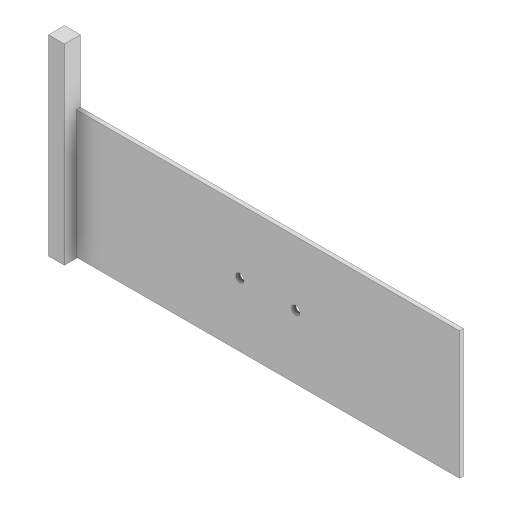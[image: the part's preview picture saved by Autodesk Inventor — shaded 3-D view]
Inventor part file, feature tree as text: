
AUTODESK INVENTOR PART (.ipt)
format: ipt  version: 2024.2 (Build 282272000, 272)  size: 103,936 bytes
history: native  units: in
note: dims shown in document units (in); Inventor stores cm internally (conversion verified against a paired STEP export)
features: extrude x2, sketch x2
ambient origin geometry x8: Origin, YZ Plane, XZ Plane, XY Plane, X Axis, Y Axis, Z Axis, Center Point
bodies: Solid1 (feature_tree)
feature tree (4):
  extrude  "Extrusion1"  Depth=4.0in
  extrude  "Extrusion2"  Depth=0.5in
  sketch  "Sketch1"  dims[d0=12.0in d1=4.0in]
  sketch  "Sketch2"  dims[d2=0.25in d3=0.25in d4=1.75in d5=5.125in d6=2.0in d7=0.125in d8=0.0in d9=0.5in d10=6.0in d11=0.0in d12=0.5in d13=0.0in]
